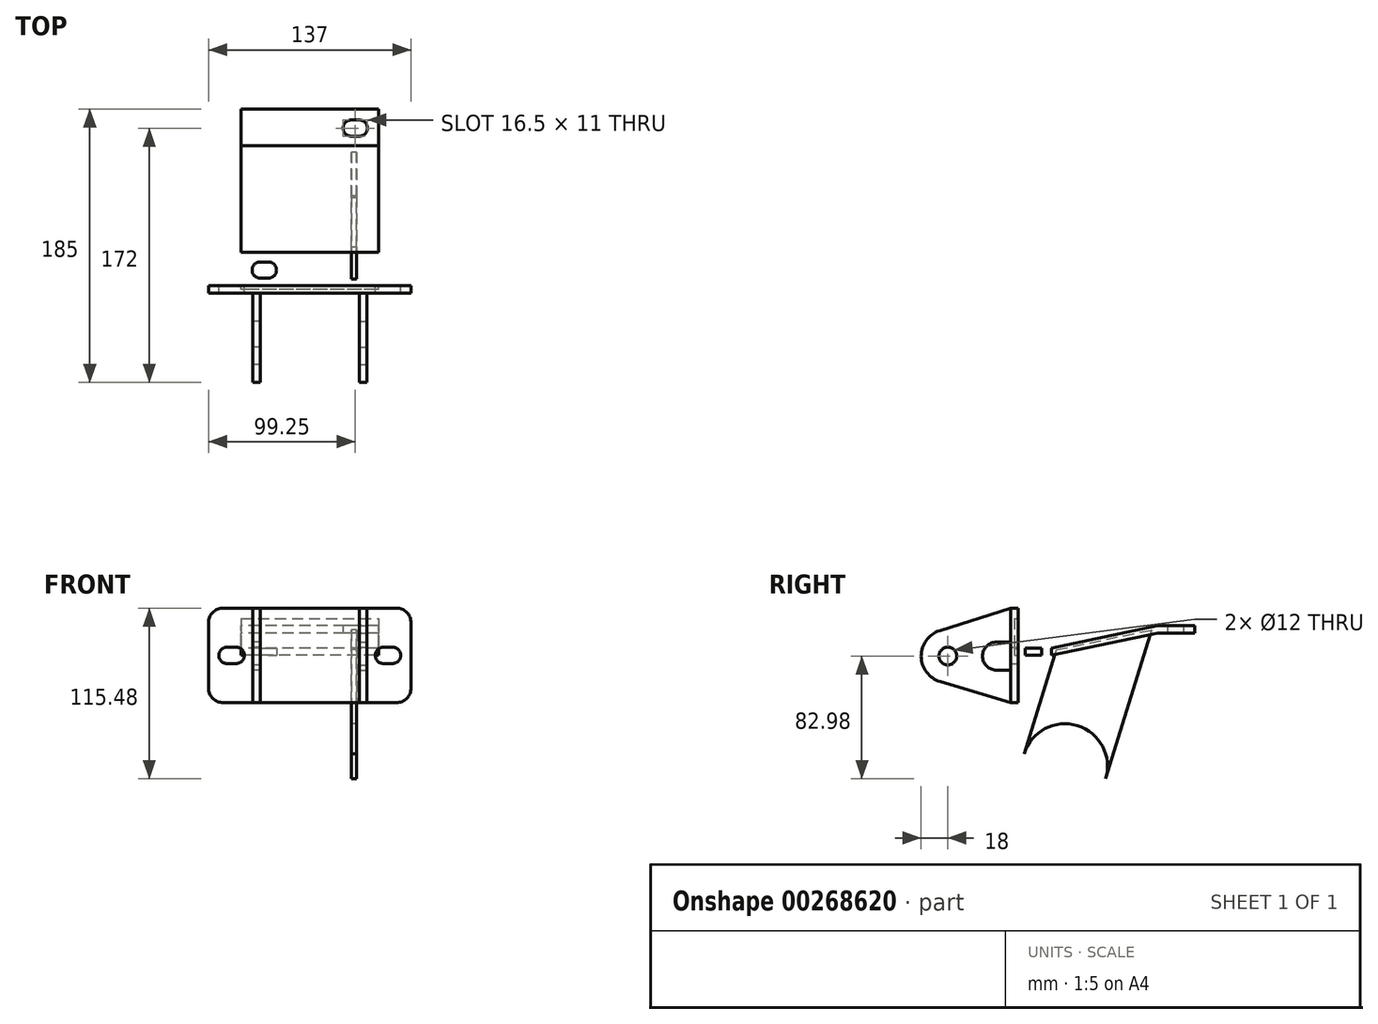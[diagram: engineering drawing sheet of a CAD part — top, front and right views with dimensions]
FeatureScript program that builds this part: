
annotation { "Feature Type Name" : "Feature", "Feature Type Description" : "" }
export const myFeature = defineFeature(function(context is Context, id is Id, definition is map)
    precondition{}
    {
        {
            var Q0;
            Q0=qCreatedBy(makeId("Front.planeOp"),FACE);
            var sketch = newSketch(context, id + "F0", { "sketchPlane" : qUnion([Q0])});
            skLineSegment(sketch, "E0.bottom", {"start": v(58.5, 32) * mm, "end": v(-58.5, 32) * mm});
            skLineSegment(sketch, "E0.top", {"start": v(58.5, -32) * mm, "end": v(-58.5, -32) * mm});
            skLineSegment(sketch, "E0.left", {"start": v(68.5, 22) * mm, "end": v(68.5, -22) * mm});
            skLineSegment(sketch, "E0.right", {"start": v(-68.5, 22) * mm, "end": v(-68.5, -22) * mm});
            skPoint(sketch, "E0.middle", {"position": v(0, 0) * mm});
            skPoint(sketch, "E1.visualSharp", {"position": v(-68.5, 32) * mm});
            skArc(sketch, "E1.filletArc", {"start": v(-58.5, 32) * mm, "mid": v(-65.57, 29.07) * mm, "end": v(-68.5, 22) * mm});
            skPoint(sketch, "E2.visualSharp", {"position": v(-68.5, -32) * mm});
            skArc(sketch, "E2.filletArc", {"start": v(-68.5, -22) * mm, "mid": v(-65.57, -29.07) * mm, "end": v(-58.5, -32) * mm});
            skPoint(sketch, "E3.visualSharp", {"position": v(68.5, -32) * mm});
            skArc(sketch, "E3.filletArc", {"start": v(58.5, -32) * mm, "mid": v(65.57, -29.07) * mm, "end": v(68.5, -22) * mm});
            skPoint(sketch, "E4.visualSharp", {"position": v(68.5, 32) * mm});
            skArc(sketch, "E4.filletArc", {"start": v(68.5, 22) * mm, "mid": v(65.57, 29.07) * mm, "end": v(58.5, 32) * mm});
            skLineSegment(sketch, "E5.bottom", {"start": v(-49.75, 5.5) * mm, "end": v(-56, 5.5) * mm});
            skLineSegment(sketch, "E5.top", {"start": v(-49.75, -5.5) * mm, "end": v(-56, -5.5) * mm});
            skPoint(sketch, "E5.middle", {"position": v(-51.84, 0) * mm});
            skArc(sketch, "E6", {"start": v(-49.75, -5.5) * mm, "mid": v(-44.25, 0) * mm, "end": v(-49.75, 5.5) * mm});
            skPoint(sketch, "E7.orphan", {"position": v(-60.34, 5.5) * mm});
            skPoint(sketch, "E8.orphan", {"position": v(-60.34, -5.5) * mm});
            skArc(sketch, "E9.trimOffspring", {"start": v(-56, 5.5) * mm, "mid": v(-61.5, 0) * mm, "end": v(-56, -5.5) * mm});
            skPoint(sketch, "E10.center.orphan", {"position": v(-54.84, 0) * mm});
            skPoint(sketch, "E11.orphan", {"position": v(-43.34, 5.5) * mm});
            skPoint(sketch, "E12.orphan", {"position": v(-43.34, -5.5) * mm});
            skArc(sketch, "E13.MirrorCS", {"start": v(49.75, -5.5) * mm, "mid": v(44.25, 0) * mm, "end": v(49.75, 5.5) * mm});
            skLineSegment(sketch, "E14.MirrorCS", {"start": v(49.75, -5.5) * mm, "end": v(56, -5.5) * mm});
            skArc(sketch, "E15.MirrorCS", {"start": v(56, 5.5) * mm, "mid": v(61.5, 0) * mm, "end": v(56, -5.5) * mm});
            skLineSegment(sketch, "E16.MirrorCS", {"start": v(49.75, 5.5) * mm, "end": v(56, 5.5) * mm});
            skSolve(sketch);
        }
        {
            var Q0;
            Q0=makeQuery(id+"F0.imprint","IMPRINT",FACE,{"disambiguationData":[TD([[makeQuery(id+"F0.imprint","IMPRINT",EDGE,{"derivedFrom":sQuery(id+"F0.wireOp",EDGE,"E0.bottom")}),1.0]])]});
            extrude(context, id + "F1", {"entities" : qUnion([Q0]), "endBound" : BoundingType.SYMMETRIC, "depth" : 5 * mm});
        }
        {
            var Q0;
            Q0=makeQuery(id+"F1.opExtrude","SWEPT_FACE",FACE,{"disambiguationData":[OSD([sQuery(id+"F0.wireOp",EDGE,"E0.right")])]});
            cPlane(context, id + "F2", {"entities" : qUnion([Q0]), "cplaneType" : CPlaneType.OFFSET, "offset" : 30 * mm, "oppositeDirection" : true, "width" : 150 * mm, "height" : 150 * mm});
        }
        {
            var Q0;
            Q0=qCreatedBy(id+"F2.planeOp",FACE);
            var sketch = newSketch(context, id + "F3", { "sketchPlane" : qUnion([Q0])});
            skLineSegment(sketch, "E17", {"start": v(2.5, 32) * mm, "end": v(2.5, 9) * mm});
            skCircle(sketch, "E18", {"center": v(45, -0.5) * mm, "radius": 6 * mm});
            skArc(sketch, "E19", {"start": v(50.16, -17.75) * mm, "mid": v(63, -0.67) * mm, "end": v(50.49, 16.64) * mm});
            skLineSegment(sketch, "E20", {"start": v(2.5, -32) * mm, "end": v(50.16, -17.75) * mm});
            skLineSegment(sketch, "E21", {"start": v(2.5, 32) * mm, "end": v(50.49, 16.64) * mm});
            skLineSegment(sketch, "E22.left", {"start": v(12, -10) * mm, "end": v(2.5, -10) * mm});
            skLineSegment(sketch, "E22.right", {"start": v(12, 9) * mm, "end": v(2.5, 9) * mm});
            skPoint(sketch, "E22.middle", {"position": v(0, -17.12) * mm});
            skArc(sketch, "E23", {"start": v(12, -10) * mm, "mid": v(21.5, -0.5) * mm, "end": v(12, 9) * mm});
            skLineSegment(sketch, "E24.trimOffspring", {"start": v(2.5, -10) * mm, "end": v(2.5, -32) * mm});
            skSolve(sketch);
        }
        {
            var Q0;
            Q0=makeQuery(id+"F3.imprint","IMPRINT",FACE,{"disambiguationData":[TD([[makeQuery(id+"F3.imprint","IMPRINT",EDGE,{"derivedFrom":sQuery(id+"F3.wireOp",EDGE,"E17")}),1.0]])]});
            extrude(context, id + "F4", {"entities" : qUnion([Q0]), "operationType" : NewBodyOperationType.ADD, "oppositeDirection" : true, "depth" : 5 * mm});
        }
        {
            var Q0;
            Q0=makeQuery(id+"F1.opExtrude","SWEPT_BODY",BODY,{"disambiguationData":[OSD([sQuery(id+"F0.wireOp",EDGE,"E0.bottom"),sQuery(id+"F0.wireOp",EDGE,"E0.top"),sQuery(id+"F0.wireOp",EDGE,"E0.left"),sQuery(id+"F0.wireOp",EDGE,"E0.right"),sQuery(id+"F0.wireOp",EDGE,"E1.filletArc"),sQuery(id+"F0.wireOp",EDGE,"E2.filletArc"),sQuery(id+"F0.wireOp",EDGE,"E3.filletArc"),sQuery(id+"F0.wireOp",EDGE,"E4.filletArc"),sQuery(id+"F0.wireOp",EDGE,"E5.bottom"),sQuery(id+"F0.wireOp",EDGE,"E5.top"),sQuery(id+"F0.wireOp",EDGE,"E6"),sQuery(id+"F0.wireOp",EDGE,"E9.trimOffspring"),sQuery(id+"F0.wireOp",EDGE,"E13.MirrorCS"),sQuery(id+"F0.wireOp",EDGE,"E14.MirrorCS"),sQuery(id+"F0.wireOp",EDGE,"E15.MirrorCS"),sQuery(id+"F0.wireOp",EDGE,"E16.MirrorCS")])]});
            var Q1;
            Q1=qCreatedBy(makeId("Right.planeOp"),FACE);
            mirror(context, id + "F5", {"operationType" : NewBodyOperationType.ADD, "entities" : qUnion([Q0]), "mirrorPlane" : qUnion([Q1])});
        }
        {
            var Q0;
            Q0=qCreatedBy(makeId("Right.planeOp"),FACE);
            var sketch = newSketch(context, id + "F6", { "sketchPlane" : qUnion([Q0])});
            skLineSegment(sketch, "E25", {"start": v(0, 0) * mm, "end": v(25, 0) * mm});
            skLineSegment(sketch, "E26", {"start": v(25, 0) * mm, "end": v(97, 15) * mm});
            skLineSegment(sketch, "E27", {"start": v(97, 15) * mm, "end": v(122, 15) * mm});
            skLineSegment(sketch, "E28", {"start": v(0, 0) * mm, "end": v(0, 5) * mm});
            skLineSegment(sketch, "E29", {"start": v(0, 5) * mm, "end": v(25, 5) * mm});
            skLineSegment(sketch, "E30", {"start": v(25, 5) * mm, "end": v(97, 20) * mm});
            skLineSegment(sketch, "E31", {"start": v(97, 20) * mm, "end": v(122, 20) * mm});
            skLineSegment(sketch, "E32", {"start": v(122, 20) * mm, "end": v(122, 15) * mm});
            skSolve(sketch);
        }
        {
            var Q0;
            Q0=makeQuery(id+"F6.imprint","IMPRINT",FACE,{"disambiguationData":[TD([[makeQuery(id+"F6.imprint","IMPRINT",EDGE,{"derivedFrom":sQuery(id+"F6.wireOp",EDGE,"E25")}),1.0]])]});
            extrude(context, id + "F7", {"entities" : qUnion([Q0]), "endBound" : BoundingType.SYMMETRIC, "depth" : 93 * mm});
        }
        {
            var Q0;
            Q0=makeQuery(id+"F7.opExtrude","SWEPT_FACE",FACE,{"disambiguationData":[OSD([sQuery(id+"F6.wireOp",EDGE,"E25")])]});
            var sketch = newSketch(context, id + "F8", { "sketchPlane" : qUnion([Q0])});
            skLineSegment(sketch, "E33.bottom", {"start": v(28, -18.5) * mm, "end": v(33.5, -18.5) * mm});
            skLineSegment(sketch, "E33.top", {"start": v(28, -7.5) * mm, "end": v(33.5, -7.5) * mm});
            skPoint(sketch, "E33.middle", {"position": v(30.75, -13) * mm});
            skArc(sketch, "E34", {"start": v(33.5, -18.5) * mm, "mid": v(39, -13) * mm, "end": v(33.5, -7.5) * mm});
            skArc(sketch, "E35", {"start": v(28, -7.5) * mm, "mid": v(22.5, -13) * mm, "end": v(28, -18.5) * mm});
            skPoint(sketch, "E36.orphan", {"position": v(39, -18.5) * mm});
            skPoint(sketch, "E37.orphan", {"position": v(39, -7.5) * mm});
            skPoint(sketch, "E38.orphan", {"position": v(22.5, -18.5) * mm});
            skPoint(sketch, "E33.left.end.orphan", {"position": v(22.5, -7.5) * mm});
            skLineSegment(sketch, "E39.bottom", {"start": v(28, -114.5) * mm, "end": v(33.5, -114.5) * mm});
            skLineSegment(sketch, "E39.top", {"start": v(28, -103.5) * mm, "end": v(33.5, -103.5) * mm});
            skPoint(sketch, "E39.middle", {"position": v(30.75, -109) * mm});
            skPoint(sketch, "E39.middle.positionSnap0", {"position": v(30.75, -18.5) * mm});
            skPoint(sketch, "E39.centerSnap0", {"position": v(30.75, -18.5) * mm});
            skArc(sketch, "E40", {"start": v(28, -103.5) * mm, "mid": v(22.5, -109) * mm, "end": v(28, -114.5) * mm});
            skPoint(sketch, "E40.centerSnap0", {"position": v(39, -109) * mm});
            skPoint(sketch, "E41.orphan", {"position": v(22.5, -114.5) * mm});
            skPoint(sketch, "E42.orphan", {"position": v(22.5, -103.5) * mm});
            skPoint(sketch, "E43.orphan", {"position": v(39, -114.5) * mm});
            skPoint(sketch, "E39.right.end.orphan", {"position": v(39, -103.5) * mm});
            skPoint(sketch, "E44.center.orphan", {"position": v(33.5, -109) * mm});
            skArc(sketch, "E45", {"start": v(33.5, -114.5) * mm, "mid": v(39, -109) * mm, "end": v(33.5, -103.5) * mm});
            skArc(sketch, "E46.MirrorCS", {"start": v(-28, -7.5) * mm, "mid": v(-22.5, -13) * mm, "end": v(-28, -18.5) * mm});
            skLineSegment(sketch, "E47.MirrorCS", {"start": v(-28, -18.5) * mm, "end": v(-33.5, -18.5) * mm});
            skLineSegment(sketch, "E48.MirrorCS", {"start": v(-28, -7.5) * mm, "end": v(-33.5, -7.5) * mm});
            skArc(sketch, "E49.MirrorCS", {"start": v(-33.5, -18.5) * mm, "mid": v(-39, -13) * mm, "end": v(-33.5, -7.5) * mm});
            skArc(sketch, "E50.MirrorCS", {"start": v(-28, -103.5) * mm, "mid": v(-22.5, -109) * mm, "end": v(-28, -114.5) * mm});
            skLineSegment(sketch, "E51.MirrorCS", {"start": v(-28, -114.5) * mm, "end": v(-33.5, -114.5) * mm});
            skLineSegment(sketch, "E52.MirrorCS", {"start": v(-28, -103.5) * mm, "end": v(-33.5, -103.5) * mm});
            skArc(sketch, "E53.MirrorCS", {"start": v(-33.5, -114.5) * mm, "mid": v(-39, -109) * mm, "end": v(-33.5, -103.5) * mm});
            skSolve(sketch);
        }
        {
            var Q0;
            Q0=makeQuery(id+"F8.imprint","IMPRINT",FACE,{"disambiguationData":[TD([[makeQuery(id+"F8.imprint","IMPRINT",EDGE,{"derivedFrom":sQuery(id+"F8.wireOp",EDGE,"E39.bottom")}),1.0]])]});
            var Q1;
            Q1=makeQuery(id+"F8.imprint","IMPRINT",FACE,{"disambiguationData":[TD([[makeQuery(id+"F8.imprint","IMPRINT",EDGE,{"derivedFrom":sQuery(id+"F8.wireOp",EDGE,"E50.MirrorCS")}),-1.0]])]});
            var Q2;
            Q2=makeQuery(id+"F8.imprint","IMPRINT",FACE,{"disambiguationData":[TD([[makeQuery(id+"F8.imprint","IMPRINT",EDGE,{"derivedFrom":sQuery(id+"F8.wireOp",EDGE,"E33.bottom")}),1.0]])]});
            var Q3;
            Q3=makeQuery(id+"F8.imprint","IMPRINT",FACE,{"disambiguationData":[TD([[makeQuery(id+"F8.imprint","IMPRINT",EDGE,{"derivedFrom":sQuery(id+"F8.wireOp",EDGE,"E46.MirrorCS")}),-1.0]])]});
            extrude(context, id + "F9", {"entities" : qUnion([Q0, Q1, Q2, Q3]), "operationType" : NewBodyOperationType.REMOVE, "oppositeDirection" : true, "depth" : 25 * mm});
        }
        {
            var Q0;
            Q0=qCreatedBy(makeId("Right.planeOp"),FACE);
            var sketch = newSketch(context, id + "F10", { "sketchPlane" : qUnion([Q0])});
            skLineSegment(sketch, "E54", {"start": v(28.5, 3.81) * mm, "end": v(92.8, 17.21) * mm});
            skLineSegment(sketch, "E55", {"start": v(92.8, 17.21) * mm, "end": v(61.72, -83.48) * mm});
            skArc(sketch, "E56", {"start": v(61.72, -83.48) * mm, "mid": v(42.73, -47.53) * mm, "end": v(6.78, -66.52) * mm});
            skLineSegment(sketch, "E57", {"start": v(6.78, -66.52) * mm, "end": v(28.5, 3.81) * mm});
            skSolve(sketch);
        }
        {
            var Q0;
            Q0=makeQuery(id+"F10.imprint","IMPRINT",FACE,{"disambiguationData":[TD([[makeQuery(id+"F10.imprint","IMPRINT",EDGE,{"derivedFrom":sQuery(id+"F10.wireOp",EDGE,"E54")}),-1.0]])]});
            extrude(context, id + "F11", {"entities" : qUnion([Q0]), "endBound" : BoundingType.SYMMETRIC, "depth" : 3.5 * mm});
        }
        {
            var Q0;
            Q0=makeQuery(id+"F11.opExtrude","SWEPT_BODY",BODY,{"disambiguationData":[OSD([sQuery(id+"F10.wireOp",EDGE,"E54"),sQuery(id+"F10.wireOp",EDGE,"E55"),sQuery(id+"F10.wireOp",EDGE,"E56"),sQuery(id+"F10.wireOp",EDGE,"E57")])]});
            transform(context, id + "F12", {"entities" : qUnion([Q0]), "transformType" : TransformType.TRANSLATION_3D, "dx" : 30 * mm, "dy" : 0 * mm, "dz" : 0 * mm, "makeCopy" : false});
        }
    });
